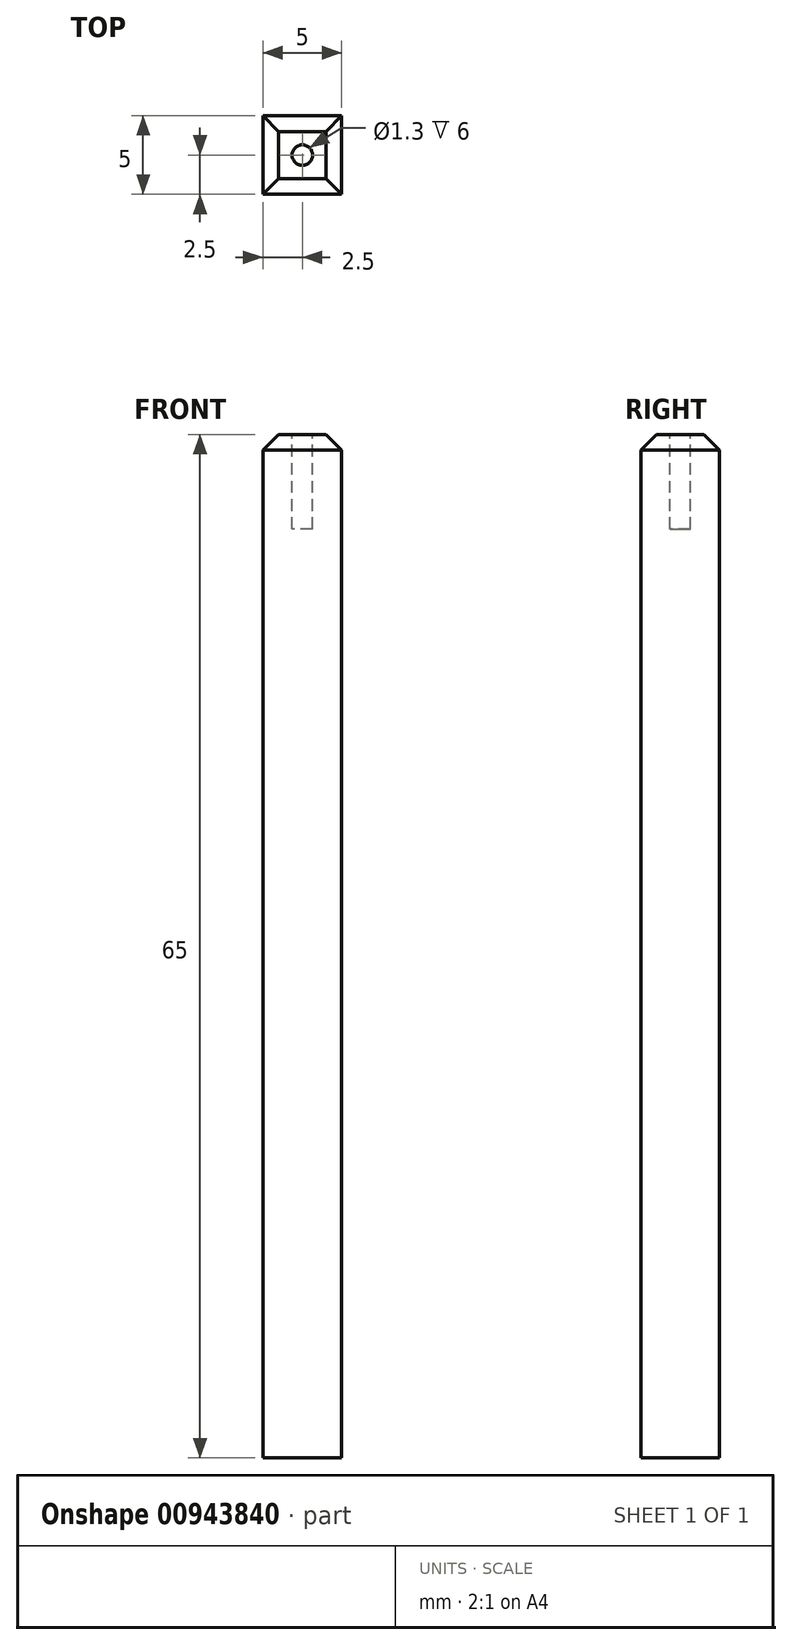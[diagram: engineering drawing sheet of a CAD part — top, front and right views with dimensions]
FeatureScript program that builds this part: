
annotation { "Feature Type Name" : "Feature", "Feature Type Description" : "" }
export const myFeature = defineFeature(function(context is Context, id is Id, definition is map)
    precondition{}
    {
        {
            var Q0;
            Q0=qCreatedBy(makeId("Top.planeOp"),FACE);
            var sketch = newSketch(context, id + "F0", { "sketchPlane" : qUnion([Q0])});
            skLineSegment(sketch, "E0.bottom", {"start": v(2.5, -2.5) * mm, "end": v(-2.5, -2.5) * mm});
            skLineSegment(sketch, "E0.top", {"start": v(2.5, 2.5) * mm, "end": v(-2.5, 2.5) * mm});
            skLineSegment(sketch, "E0.left", {"start": v(2.5, -2.5) * mm, "end": v(2.5, 2.5) * mm});
            skLineSegment(sketch, "E0.right", {"start": v(-2.5, -2.5) * mm, "end": v(-2.5, 2.5) * mm});
            skPoint(sketch, "E0.middle", {"position": v(0, 0) * mm});
            skSolve(sketch);
        }
        {
            var Q0;
            Q0 = qSketchRegion(id + "F0", true);
            extrude(context, id + "F1", {"entities" : qUnion([Q0]), "depth" : 65 * mm, "offsetDistance" : 25 * mm});
        }
        {
            var Q0;
            Q0=makeQuery(id+"F1.opExtrude","CAP_EDGE",EDGE,{"disambiguationData":[OSD([sQuery(id+"F0.wireOp",EDGE,"E0.bottom")])],"isStart":false});
            var Q1;
            Q1=makeQuery(id+"F1.opExtrude","CAP_EDGE",EDGE,{"disambiguationData":[OSD([sQuery(id+"F0.wireOp",EDGE,"E0.left")])],"isStart":false});
            var Q2;
            Q2=makeQuery(id+"F1.opExtrude","CAP_EDGE",EDGE,{"disambiguationData":[OSD([sQuery(id+"F0.wireOp",EDGE,"E0.top")])],"isStart":false});
            var Q3;
            Q3=makeQuery(id+"F1.opExtrude","CAP_EDGE",EDGE,{"disambiguationData":[OSD([sQuery(id+"F0.wireOp",EDGE,"E0.right")])],"isStart":false});
            chamfer(context, id + "F2", {"entities" : qUnion([Q0, Q1, Q2, Q3]), "width" : 1 * mm, "tangentPropagation" : true});
        }
        {
            var Q0;
            Q0=makeQuery(id+"F1.opExtrude","CAP_FACE",FACE,{"disambiguationData":[OSD([sQuery(id+"F0.wireOp",EDGE,"E0.bottom"),sQuery(id+"F0.wireOp",EDGE,"E0.top"),sQuery(id+"F0.wireOp",EDGE,"E0.left"),sQuery(id+"F0.wireOp",EDGE,"E0.right")])],"isStart":false});
            var sketch = newSketch(context, id + "F3", { "sketchPlane" : qUnion([Q0])});
            skCircle(sketch, "E1", {"center": v(0, 0) * mm, "radius": 0.65 * mm});
            skSolve(sketch);
        }
        {
            var Q0;
            Q0 = qSketchRegion(id + "F3", true);
            extrude(context, id + "F4", {"entities" : qUnion([Q0]), "operationType" : NewBodyOperationType.REMOVE, "oppositeDirection" : true, "depth" : 6 * mm, "offsetDistance" : 25 * mm});
        }
    });
